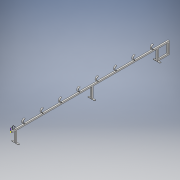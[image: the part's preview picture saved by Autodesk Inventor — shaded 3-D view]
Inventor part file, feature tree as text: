
AUTODESK INVENTOR PART (.ipt)
format: ipt  version: 2017 (Build 210142000, 142)  size: 224,256 bytes
history: native  units: mm
features: sketch x8, extrude x7, pattern_linear x3
ambient origin geometry x8: Origin, YZ Plane, XZ Plane, XY Plane, X Axis, Y Axis, Z Axis, Center Point
bodies: Solid1 (feature_tree)
feature tree (18):
  extrude  "Extrusion1"  Depth=2900.0mm
  extrude  "Extrusion2"  Depth=25.0mm
  extrude  "Extrusion3"  Depth=25.0mm
  extrude  "Extrusion4"  Depth=25.0mm
  extrude  "Extrusion5"  Depth=5.0mm
  pattern_linear  "Rectangular Pattern1"  Count1=5 Spacing1=75.0mm
  extrude  "Extrusion6"  Depth=5.0mm
  pattern_linear  "Rectangular Pattern2"  Count1=5 Spacing1=75.0mm
  extrude  "Extrusion7"  Depth=42.0mm
  pattern_linear  "Rectangular Pattern3"  Spacing1=25.0mm  [1 undecoded]
  sketch  "Sketch10"  dims[d27=20.0mm d29=1404.0mm d31=4.0mm d32=25.0mm d33=0.0mm d34=80.0mm d36=338.0mm d39=42.0mm d40=290.0mm d41=42.0mm]
  sketch  "Sketch1"  dims[d0=25.0mm d1=2900.0mm]
  sketch  "Sketch2"  dims[d2=25.0mm d3=0.0mm d4=25.0mm]
  sketch  "Sketch3"  dims[d5=200.0mm d6=0.0mm d7=25.0mm]
  sketch  "Sketch4"  dims[d8=200.0mm d9=0.0mm d10=25.0mm]
  sketch  "Sketch6"  dims[d11=200.0mm d12=0.0mm d13=5.0mm]
  sketch  "Sketch7"  dims[d14=25.0mm d15=50.0mm d16=75.0mm d17=0.0mm d18=0.0mm]
  sketch  "Sketch8"  dims[d19=30.0mm d21=1404.0mm d22=5.0mm d23=50.0mm d24=75.0mm d25=0.0mm d26=0.0mm]
note: 1 required parameter value undecoded (feature->parameter linkage not recoverable at this tier; creation-order binding heuristic only, values carry confidence <= 0.55)
